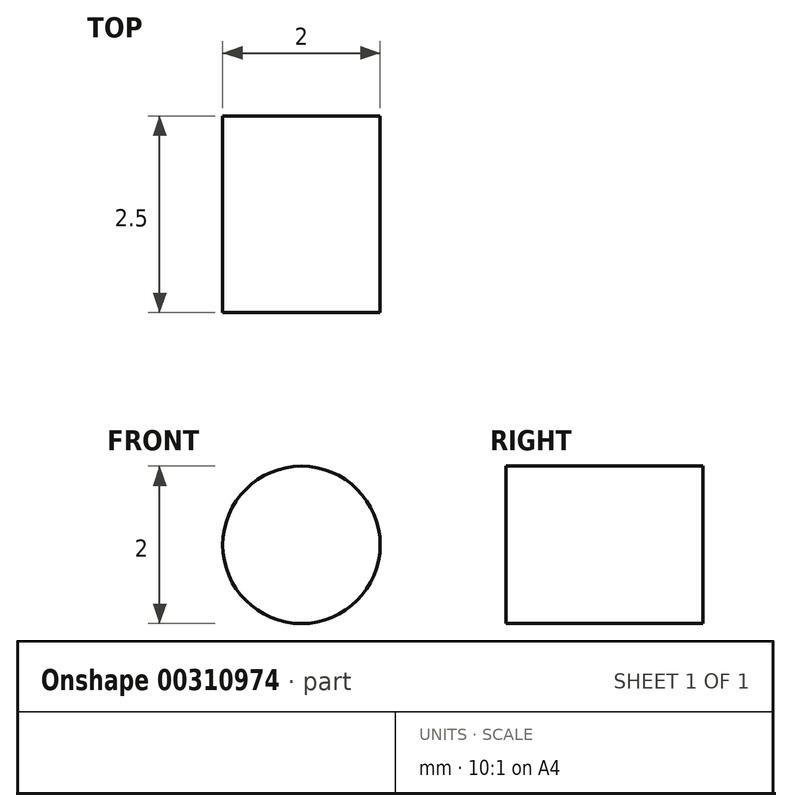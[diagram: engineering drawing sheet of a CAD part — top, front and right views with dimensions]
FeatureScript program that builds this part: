
annotation { "Feature Type Name" : "Feature", "Feature Type Description" : "" }
export const myFeature = defineFeature(function(context is Context, id is Id, definition is map)
    precondition{}
    {
        {
            var Q0;
            Q0=qCreatedBy(makeId("Front.planeOp"),FACE);
            var sketch = newSketch(context, id + "F0", { "sketchPlane" : qUnion([Q0])});
            skCircle(sketch, "E0", {"center": v(0, 0) * mm, "radius": 1 * mm});
            skSolve(sketch);
        }
        {
            var Q0;
            Q0=makeQuery(id+"F0.imprint","IMPRINT",FACE,{"disambiguationData":[TD([[makeQuery(id+"F0.imprint","IMPRINT",EDGE,{"derivedFrom":sQuery(id+"F0.wireOp",EDGE,"E0")}),1.0]])]});
            extrude(context, id + "F1", {"entities" : qUnion([Q0]), "depth" : 2.5 * mm});
        }
    });
